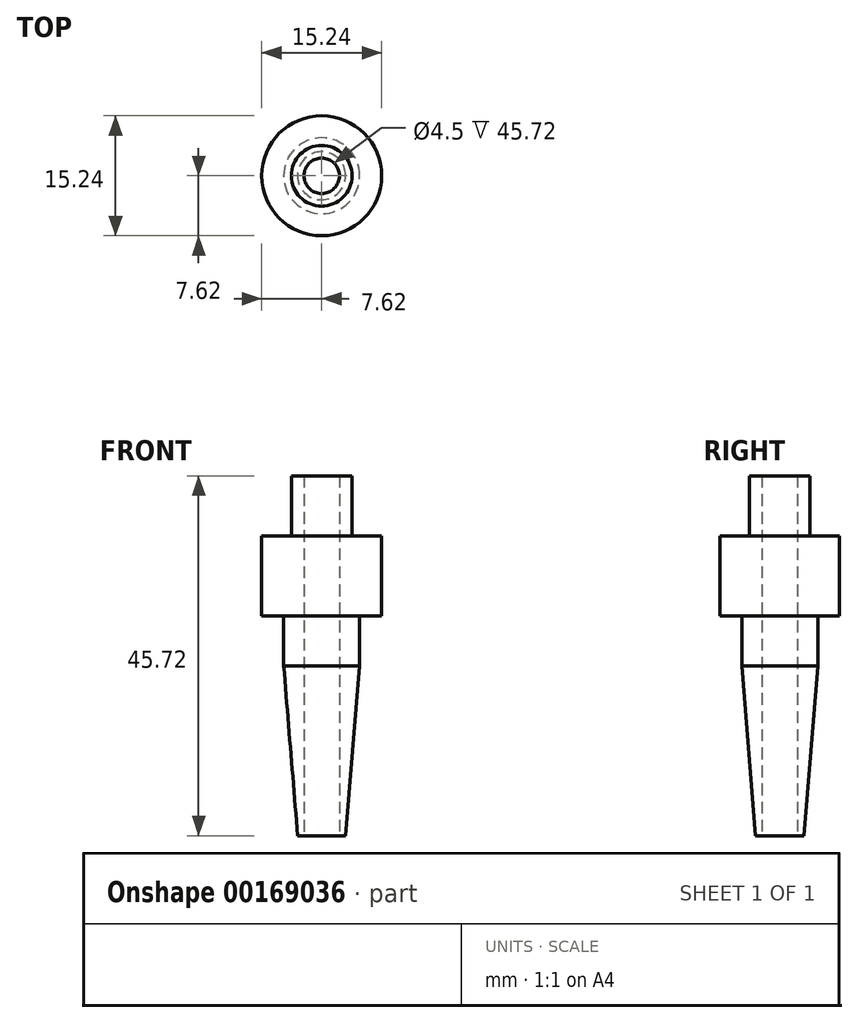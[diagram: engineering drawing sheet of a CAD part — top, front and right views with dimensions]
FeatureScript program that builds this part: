
annotation { "Feature Type Name" : "Feature", "Feature Type Description" : "" }
export const myFeature = defineFeature(function(context is Context, id is Id, definition is map)
    precondition{}
    {
        {
            var Q0;
            Q0=qCreatedBy(makeId("Front.planeOp"),FACE);
            var sketch = newSketch(context, id + "F0", { "sketchPlane" : qUnion([Q0])});
            skLineSegment(sketch, "E0", {"start": v(0, 0) * mm, "end": v(0, 73.29) * mm});
            skSolve(sketch);
        }
        {
            var Q0;
            Q0=qCreatedBy(makeId("Front.planeOp"),FACE);
            var sketch = newSketch(context, id + "F1", { "sketchPlane" : qUnion([Q0])});
            skLineSegment(sketch, "E1", {"start": v(2.25, 45.72) * mm, "end": v(2.25, 0) * mm});
            skLineSegment(sketch, "E2", {"start": v(2.25, 0) * mm, "end": v(3.05, 0) * mm});
            skLineSegment(sketch, "E3", {"start": v(4.83, 21.59) * mm, "end": v(4.83, 27.94) * mm});
            skLineSegment(sketch, "E4", {"start": v(4.83, 27.94) * mm, "end": v(7.62, 27.94) * mm});
            skLineSegment(sketch, "E5", {"start": v(7.62, 27.94) * mm, "end": v(7.62, 38.1) * mm});
            skLineSegment(sketch, "E6", {"start": v(4.83, 21.59) * mm, "end": v(3.05, 0) * mm});
            skLineSegment(sketch, "E7", {"start": v(3.85, 45.72) * mm, "end": v(3.85, 38.1) * mm});
            skLineSegment(sketch, "E8", {"start": v(2.25, 45.72) * mm, "end": v(3.85, 45.72) * mm});
            skLineSegment(sketch, "E9", {"start": v(3.85, 38.1) * mm, "end": v(7.62, 38.1) * mm});
            skSolve(sketch);
        }
        {
            var Q0;
            Q0 = qSketchRegion(id + "F1", true);
            var Q1;
            Q1=sQuery(id+"F0.wireOp",EDGE,"E0");
            revolve(context, id + "F2", {"entities" : qUnion([Q0]), "axis" : qUnion([Q1]), "revolveType" : RevolveType.FULL});
        }
    });
